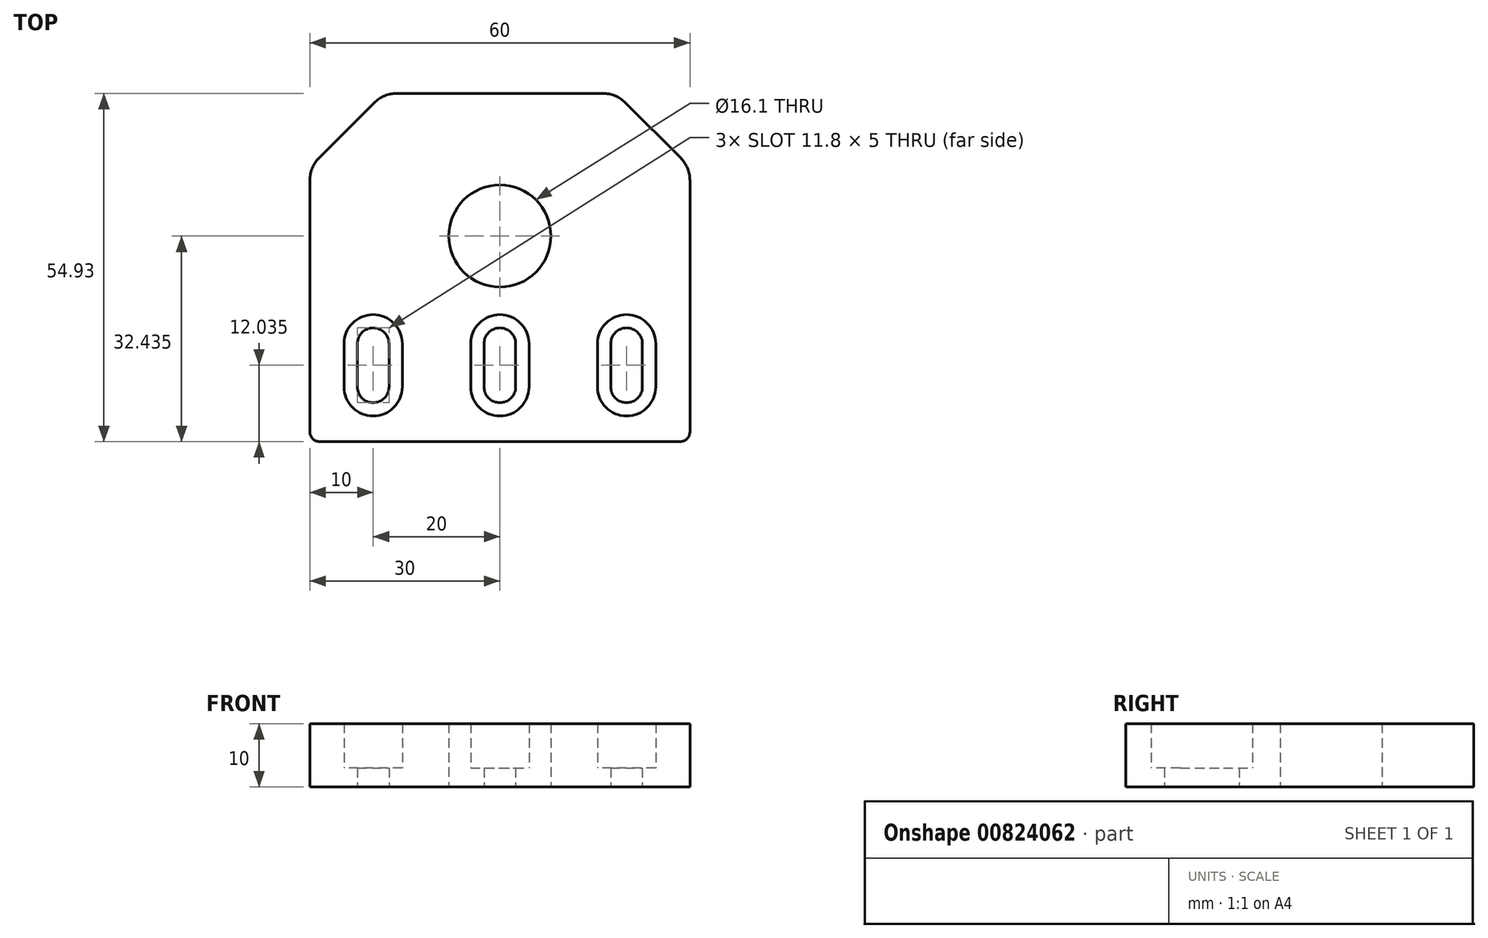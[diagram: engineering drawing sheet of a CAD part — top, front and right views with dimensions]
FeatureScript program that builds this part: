
annotation { "Feature Type Name" : "Feature", "Feature Type Description" : "" }
export const myFeature = defineFeature(function(context is Context, id is Id, definition is map)
    precondition{}
    {
        {
            var Q0;
            Q0=qCreatedBy(makeId("Top.planeOp"),FACE);
            var sketch = newSketch(context, id + "F0", { "sketchPlane" : qUnion([Q0])});
            skLineSegment(sketch, "E0", {"start": v(-19.81, 26) * mm, "end": v(-28.54, 17.28) * mm});
            skLineSegment(sketch, "E1", {"start": v(-30, 13.74) * mm, "end": v(-30, -25.96) * mm});
            skLineSegment(sketch, "E2", {"start": v(-28.5, -27.46) * mm, "end": v(28.5, -27.46) * mm});
            skLineSegment(sketch, "E3", {"start": v(-22.5, -18.83) * mm, "end": v(-22.5, -12.03) * mm});
            skLineSegment(sketch, "E4", {"start": v(-17.5, -12.03) * mm, "end": v(-17.5, -18.83) * mm});
            skLineSegment(sketch, "E5", {"start": v(-2.5, -18.83) * mm, "end": v(-2.5, -12.03) * mm});
            skLineSegment(sketch, "E6", {"start": v(2.5, -12.03) * mm, "end": v(2.5, -18.83) * mm});
            skLineSegment(sketch, "E7", {"start": v(17.5, -18.83) * mm, "end": v(17.5, -12.03) * mm});
            skLineSegment(sketch, "E8", {"start": v(22.5, -12.03) * mm, "end": v(22.5, -18.83) * mm});
            skLineSegment(sketch, "E9", {"start": v(16.28, 27.47) * mm, "end": v(-16.28, 27.47) * mm});
            skLineSegment(sketch, "E10", {"start": v(30, -25.96) * mm, "end": v(30, 13.74) * mm});
            skLineSegment(sketch, "E11", {"start": v(28.54, 17.28) * mm, "end": v(19.81, 26) * mm});
            skCircle(sketch, "E12", {"center": v(0, 4.97) * mm, "radius": 8.05 * mm});
            skCircle(sketch, "E13", {"center": v(0, 4.97) * mm, "radius": 5.5 * mm});
            skArc(sketch, "E14", {"start": v(30, 13.74) * mm, "mid": v(29.62, 15.66) * mm, "end": v(28.54, 17.28) * mm});
            skArc(sketch, "E15", {"start": v(19.81, 26) * mm, "mid": v(18.2, 27.08) * mm, "end": v(16.28, 27.47) * mm});
            skArc(sketch, "E16", {"start": v(-16.28, 27.47) * mm, "mid": v(-18.2, 27.08) * mm, "end": v(-19.81, 26) * mm});
            skArc(sketch, "E17", {"start": v(-28.54, 17.28) * mm, "mid": v(-29.62, 15.66) * mm, "end": v(-30, 13.74) * mm});
            skArc(sketch, "E18", {"start": v(17.5, -18.83) * mm, "mid": v(20, -21.33) * mm, "end": v(22.5, -18.83) * mm});
            skArc(sketch, "E19", {"start": v(22.5, -12.03) * mm, "mid": v(20, -9.53) * mm, "end": v(17.5, -12.03) * mm});
            skArc(sketch, "E20", {"start": v(-2.5, -18.83) * mm, "mid": v(0, -21.33) * mm, "end": v(2.5, -18.83) * mm});
            skArc(sketch, "E21", {"start": v(2.5, -12.03) * mm, "mid": v(0, -9.53) * mm, "end": v(-2.5, -12.03) * mm});
            skArc(sketch, "E22", {"start": v(-22.5, -18.83) * mm, "mid": v(-20, -21.33) * mm, "end": v(-17.5, -18.83) * mm});
            skArc(sketch, "E23", {"start": v(-17.5, -12.03) * mm, "mid": v(-20, -9.53) * mm, "end": v(-22.5, -12.03) * mm});
            skArc(sketch, "E24", {"start": v(-30, -25.96) * mm, "mid": v(-29.56, -27.03) * mm, "end": v(-28.5, -27.46) * mm});
            skArc(sketch, "E25", {"start": v(28.5, -27.46) * mm, "mid": v(29.56, -27.03) * mm, "end": v(30, -25.96) * mm});
            skLineSegment(sketch, "E26.0", {"start": v(-15.4, -12.03) * mm, "end": v(-15.4, -18.83) * mm});
            skArc(sketch, "E26.1", {"start": v(-15.4, -12.03) * mm, "mid": v(-20, -7.43) * mm, "end": v(-24.6, -12.03) * mm});
            skLineSegment(sketch, "E26.2", {"start": v(-24.6, -18.83) * mm, "end": v(-24.6, -12.03) * mm});
            skArc(sketch, "E26.3", {"start": v(-24.6, -18.83) * mm, "mid": v(-20, -23.43) * mm, "end": v(-15.4, -18.83) * mm});
            skArc(sketch, "E27.0", {"start": v(-4.6, -18.83) * mm, "mid": v(0, -23.43) * mm, "end": v(4.6, -18.83) * mm});
            skLineSegment(sketch, "E27.1", {"start": v(-4.6, -18.83) * mm, "end": v(-4.6, -12.03) * mm});
            skArc(sketch, "E27.2", {"start": v(4.6, -12.03) * mm, "mid": v(0, -7.43) * mm, "end": v(-4.6, -12.03) * mm});
            skLineSegment(sketch, "E27.3", {"start": v(4.6, -12.03) * mm, "end": v(4.6, -18.83) * mm});
            skArc(sketch, "E28.0", {"start": v(24.6, -12.03) * mm, "mid": v(20, -7.43) * mm, "end": v(15.4, -12.03) * mm});
            skLineSegment(sketch, "E28.1", {"start": v(24.6, -12.03) * mm, "end": v(24.6, -18.83) * mm});
            skArc(sketch, "E28.2", {"start": v(15.4, -18.83) * mm, "mid": v(20, -23.43) * mm, "end": v(24.6, -18.83) * mm});
            skLineSegment(sketch, "E28.3", {"start": v(15.4, -18.83) * mm, "end": v(15.4, -12.03) * mm});
            skSolve(sketch);
        }
        {
            var Q0;
            Q0 = qSketchRegion(id + "F0", true);
            extrude(context, id + "F1", {"entities" : qUnion([Q0]), "depth" : 10 * mm, "offsetDistance" : 25 * mm});
        }
        {
            var Q0;
            Q0=makeQuery(id+"F0.imprint","IMPRINT",FACE,{"disambiguationData":[TD([[makeQuery(id+"F0.imprint","IMPRINT",EDGE,{"derivedFrom":sQuery(id+"F0.wireOp",EDGE,"E3")}),1.0]])]});
            var Q1;
            Q1=makeQuery(id+"F0.imprint","IMPRINT",FACE,{"disambiguationData":[TD([[makeQuery(id+"F0.imprint","IMPRINT",EDGE,{"derivedFrom":sQuery(id+"F0.wireOp",EDGE,"E5")}),1.0]])]});
            var Q2;
            Q2=makeQuery(id+"F0.imprint","IMPRINT",FACE,{"disambiguationData":[TD([[makeQuery(id+"F0.imprint","IMPRINT",EDGE,{"derivedFrom":sQuery(id+"F0.wireOp",EDGE,"E7")}),1.0]])]});
            extrude(context, id + "F2", {"entities" : qUnion([Q0, Q1, Q2]), "operationType" : NewBodyOperationType.ADD, "depth" : 3 * mm, "offsetDistance" : 25 * mm});
        }
    });
